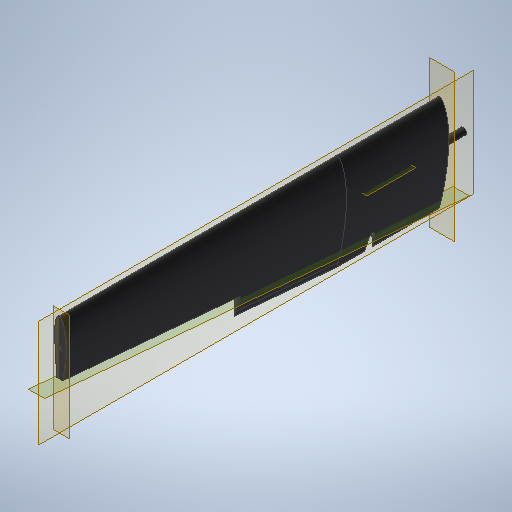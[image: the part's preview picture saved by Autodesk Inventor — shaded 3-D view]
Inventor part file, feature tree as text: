
AUTODESK INVENTOR PART (.ipt)
format: ipt  version: 2025.2 (Build 292293000, 293)  size: 489,472 bytes
history: native  units: in
note: dims shown in document units (in); Inventor stores cm internally (conversion verified against a paired STEP export)
features: extrude x12, sketch x12, plane x7, other x6, projected_geometry x4, reference x2, loft x1, mirror x1
ambient origin geometry x8: Origin, YZ Plane, XZ Plane, XY Plane, X Axis, Y Axis, Z Axis, Center Point
bodies: Solid1 (feature_tree)
feature tree (45):
  plane  "Work Plane1"
  extrude  "Extrusion1"  Depth=3.0in TaperAngle=0.0deg
  extrude  "Extrusion3"  Depth=7.382in
  plane  "Work Plane2"
  extrude  "Extrusion4"  TaperAngle=0.0deg  [1 undecoded]
  plane  "Work Plane3"
  plane  "Work Plane6"
  loft  "Loft2"
  plane  "Work Plane7"
  extrude  "Extrusion6"  Depth=9.5in
  extrude  "Extrusion7"  Depth=24.0in
  extrude  "Extrusion8"  Depth=1.75in TaperAngle=0.0deg
  extrude  "Extrusion9"  Depth=1.2205in
  extrude  "Extrusion10"  Depth=0.2559in TaperAngle=0.0deg
  extrude  "Extrusion11"  Depth=0.2559in TaperAngle=0.0deg
  plane  "Work Plane8"
  mirror  "Mirror1"
  extrude  "Extrusion12"  Depth=0.9055in
  extrude  "Extrusion13"  Depth=0.5in TaperAngle=0.0deg
  extrude  "Extrusion14"  Depth=0.5in
  sketch  "Sketch1"  dims[d0=13.7795in d1=0.0in d4=3.0in d5=0.0in]
  reference  "Reference1"
  sketch  "Sketch3"  dims[d6=37.4016in d7=7.382in]
  reference  "Reference3"
  sketch  "Sketch4"  dims[d8=0.1in d9=0.0in d15=0.0in]
  projected_geometry  "Projected Loop2"
  plane  "Work Plane5"
  other  "Edges3"
  other  "Edges4"
  sketch  "Sketch8"  dims[d16=0.0in d17=90.0deg d18=0.0in d19=90.0deg]
  sketch  "Sketch9"  dims[d24=1.125in d25=9.5in]
  sketch  "Sketch10"  dims[d26=0.0in d27=0.0in d28=24.0in]
  sketch  "Sketch11"  dims[d29=2.5in d30=1.75in d31=0.0in]
  sketch  "Sketch12"  dims[d32=0.4724in d33=1.2205in]
  projected_geometry  "Projected Loop4"
  sketch  "Sketch13"  dims[d34=0.125in d35=0.2559in d36=0.0in]
  projected_geometry  "Projected Loop5"
  sketch  "Sketch14"  dims[d37=2.0in d38=0.2559in d39=0.0in]
  sketch  "Sketch15"  dims[d40=0.4724in d41=0.9055in]
  projected_geometry  "Projected Loop6"
  sketch  "Sketch16"  dims[d44=0.0in d45=0.8268in d46=0.0in d49=0.0984in d50=0.0984in d51=0.0787in d52=0.0787in d53=100.0in d54=0.0in d55=0.5in d56=0.5in d57=0.5in d58=0.0in d59=1.06in d60=48.0in d61=0.0in d62=3.0in d63=-0.0069in d64=0.0in d20=0.5in d21=0.0344in d22=0.5in d23=0.0344in]
  other  "Wing.iam"
  other  "WingBox:1"
  other  "UAV_Assembly.iam"
  other  "Boom:1"
note: 1 required parameter value undecoded (feature->parameter linkage not recoverable at this tier; creation-order binding heuristic only, values carry confidence <= 0.55)
